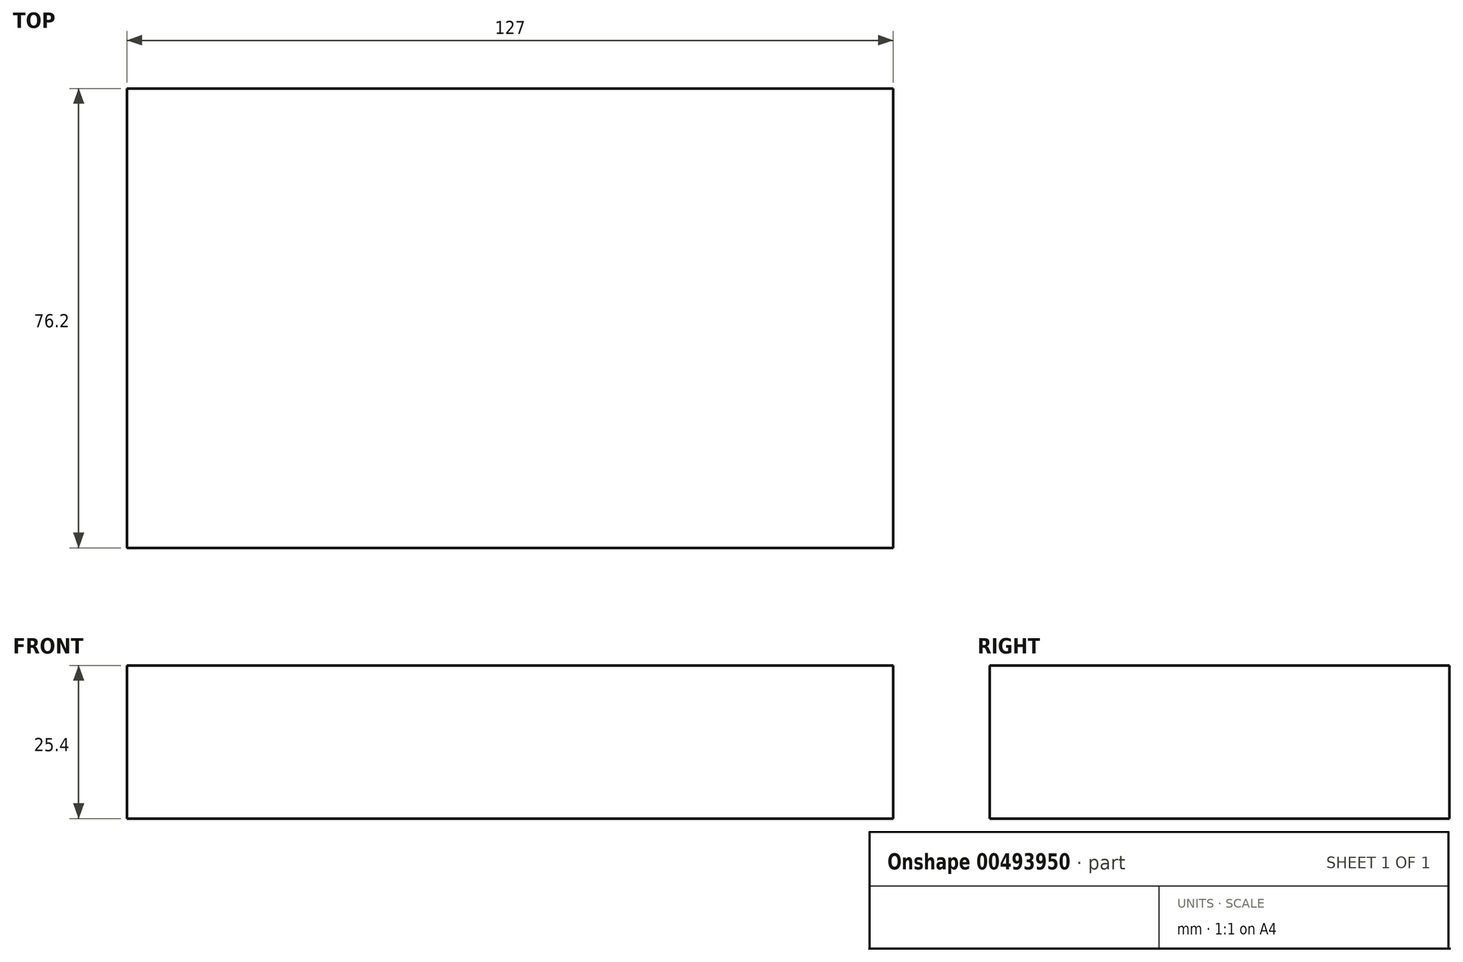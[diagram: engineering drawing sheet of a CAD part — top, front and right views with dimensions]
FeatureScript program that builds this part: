
annotation { "Feature Type Name" : "Feature", "Feature Type Description" : "" }
export const myFeature = defineFeature(function(context is Context, id is Id, definition is map)
    precondition{}
    {
        {
            var Q0;
            Q0=qCreatedBy(makeId("Top.planeOp"),FACE);
            var sketch = newSketch(context, id + "F0", { "sketchPlane" : qUnion([Q0])});
            skLineSegment(sketch, "E0", {"start": v(-63.82, 47.52) * mm, "end": v(-63.82, -28.68) * mm});
            skLineSegment(sketch, "E1", {"start": v(-63.82, -28.68) * mm, "end": v(63.18, -28.68) * mm});
            skLineSegment(sketch, "E2", {"start": v(63.18, -28.68) * mm, "end": v(63.18, 47.52) * mm});
            skLineSegment(sketch, "E3", {"start": v(63.18, 47.52) * mm, "end": v(-63.82, 47.52) * mm});
            skSolve(sketch);
        }
        {
            var Q0;
            Q0=makeQuery(id+"F0.imprint","IMPRINT",FACE,{"disambiguationData":[TD([[makeQuery(id+"F0.imprint","IMPRINT",EDGE,{"derivedFrom":sQuery(id+"F0.wireOp",EDGE,"E0")}),1.0]])]});
            extrude(context, id + "F1", {"entities" : qUnion([Q0]), "depth" : 25.4 * mm});
        }
        {
            var Q0;
            Q0=makeQuery(id+"F1.opExtrude","CAP_FACE",FACE,{"disambiguationData":[OSD([sQuery(id+"F0.wireOp",EDGE,"E0"),sQuery(id+"F0.wireOp",EDGE,"E1"),sQuery(id+"F0.wireOp",EDGE,"E2"),sQuery(id+"F0.wireOp",EDGE,"E3")])],"isStart":false});
            var sketch = newSketch(context, id + "F2", { "sketchPlane" : qUnion([Q0])});
            skLineSegment(sketch, "E4", {"start": v(-38.42, 47.52) * mm, "end": v(-38.42, -28.68) * mm});
            skLineSegment(sketch, "E5", {"start": v(12.38, 47.52) * mm, "end": v(12.38, -28.68) * mm});
            skSolve(sketch);
        }
        {
            var Q0;
            {var subQ0=sQuery(id+"F2.wireOp",EDGE,"E4");Q0=makeQuery(id+"F2.imprint","IMPRINT",FACE,{"disambiguationData":[TD([[makeQuery(id+"F2.imprint","IMPRINT",EDGE,{"derivedFrom":subQ0}),1.0]])]});}
            extrude(context, id + "F3", {"entities" : qUnion([Q0]), "operationType" : NewBodyOperationType.ADD, "depth" : -12.7 * mm});
        }
    });
